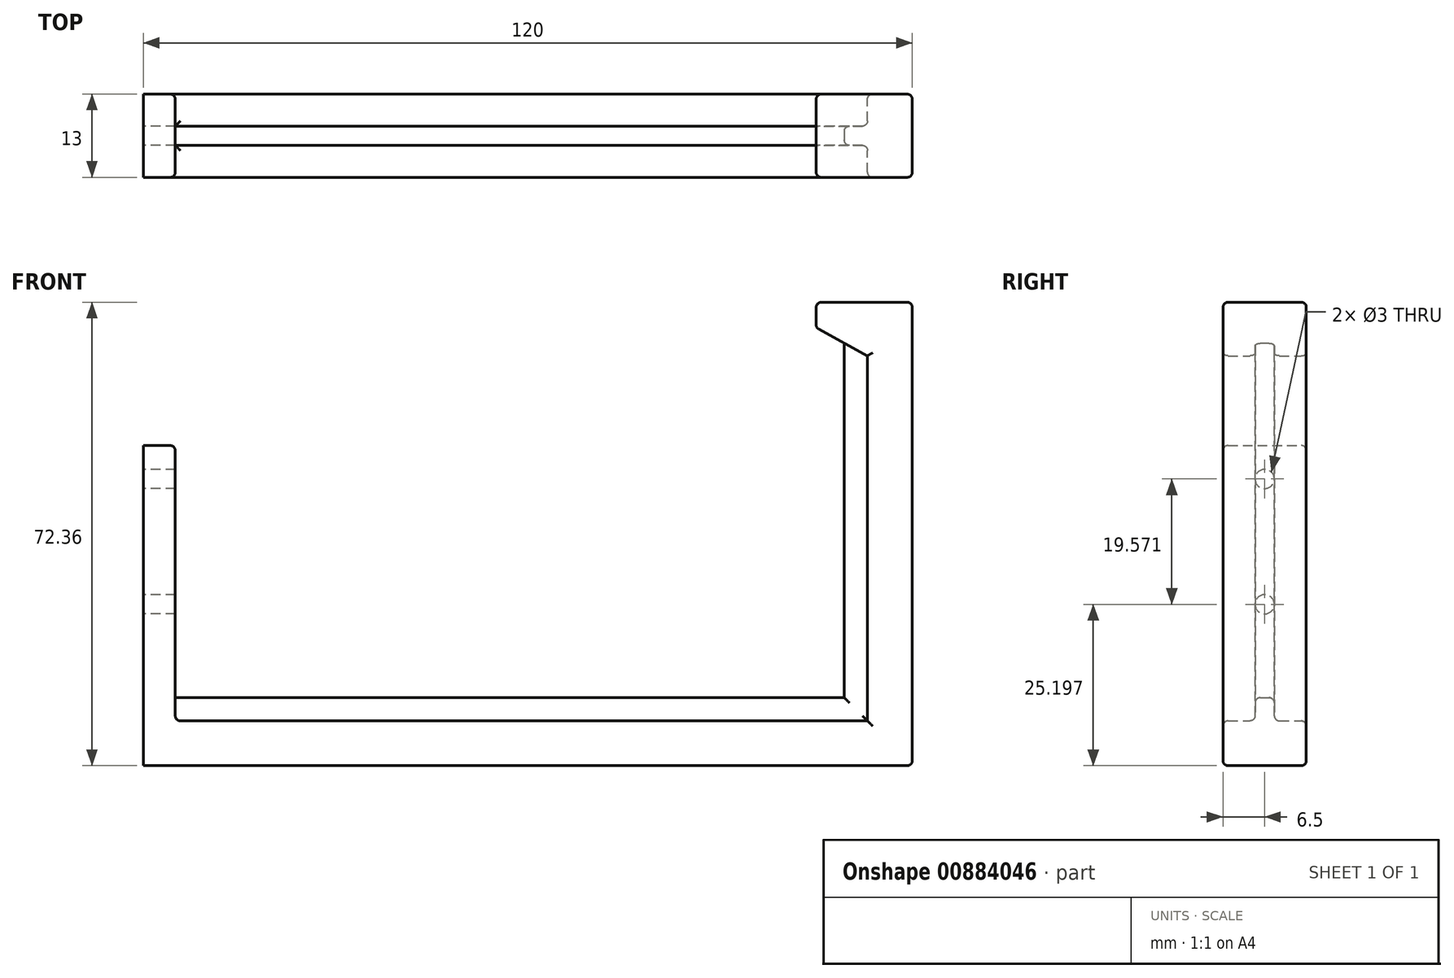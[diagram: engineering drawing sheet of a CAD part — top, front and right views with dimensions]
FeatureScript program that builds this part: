
annotation { "Feature Type Name" : "Feature", "Feature Type Description" : "" }
export const myFeature = defineFeature(function(context is Context, id is Id, definition is map)
    precondition{}
    {
        {
            var Q0;
            Q0=qCreatedBy(makeId("Front.planeOp"),FACE);
            var sketch = newSketch(context, id + "F0", { "sketchPlane" : qUnion([Q0])});
            skLineSegment(sketch, "E0", {"start": v(-72.96, 0) * mm, "end": v(-72.96, 50) * mm});
            skLineSegment(sketch, "E1", {"start": v(-72.96, 50) * mm, "end": v(-67.96, 50) * mm});
            skLineSegment(sketch, "E2", {"start": v(-67.96, 50) * mm, "end": v(-67.96, 7) * mm});
            skLineSegment(sketch, "E3", {"start": v(-67.96, 7) * mm, "end": v(40.04, 7) * mm});
            skLineSegment(sketch, "E4", {"start": v(40.04, 7) * mm, "end": v(40.04, 64) * mm});
            skLineSegment(sketch, "E5", {"start": v(40.04, 64) * mm, "end": v(32.04, 68.36) * mm});
            skLineSegment(sketch, "E6", {"start": v(32.04, 68.36) * mm, "end": v(32.04, 72.36) * mm});
            skLineSegment(sketch, "E7", {"start": v(32.04, 72.36) * mm, "end": v(47.04, 72.36) * mm});
            skLineSegment(sketch, "E8", {"start": v(47.04, 72.36) * mm, "end": v(47.04, 0) * mm});
            skLineSegment(sketch, "E9", {"start": v(47.04, 0) * mm, "end": v(-72.96, 0) * mm});
            skSolve(sketch);
        }
        {
            var Q0;
            Q0=makeQuery(id+"F0.imprint","IMPRINT",FACE,{"disambiguationData":[TD([[makeQuery(id+"F0.imprint","IMPRINT",EDGE,{"derivedFrom":sQuery(id+"F0.wireOp",EDGE,"E0")}),-1.0]])]});
            extrude(context, id + "F1", {"entities" : qUnion([Q0]), "endBound" : BoundingType.SYMMETRIC, "depth" : 13 * mm, "offsetDistance" : 25 * mm});
        }
        {
            var Q0;
            Q0=makeQuery(id+"F1.opExtrude","SWEPT_FACE",FACE,{"disambiguationData":[OSD([sQuery(id+"F0.wireOp",EDGE,"E0")])]});
            var sketch = newSketch(context, id + "F2", { "sketchPlane" : qUnion([Q0])});
            skCircle(sketch, "E10", {"center": v(0, 25.2) * mm, "radius": 1.5 * mm});
            skCircle(sketch, "E11", {"center": v(0, 44.77) * mm, "radius": 1.5 * mm});
            skSolve(sketch);
        }
        {
            var Q0;
            Q0 = qSketchRegion(id + "F2", true);
            extrude(context, id + "F3", {"entities" : qUnion([Q0]), "operationType" : NewBodyOperationType.REMOVE, "oppositeDirection" : true, "depth" : 25 * mm, "offsetDistance" : 25 * mm});
        }
        {
            var Q0;
            Q0=qCreatedBy(makeId("Front.planeOp"),FACE);
            var sketch = newSketch(context, id + "F4", { "sketchPlane" : qUnion([Q0])});
            skLineSegment(sketch, "E12", {"start": v(-71.5, 7.55) * mm, "end": v(-71.5, 5.62) * mm});
            skLineSegment(sketch, "E13", {"start": v(-71.5, 5.62) * mm, "end": v(41.44, 5.62) * mm});
            skLineSegment(sketch, "E14", {"start": v(41.44, 5.62) * mm, "end": v(41.44, 70.86) * mm});
            skLineSegment(sketch, "E15", {"start": v(41.44, 70.86) * mm, "end": v(36.44, 70.86) * mm});
            skLineSegment(sketch, "E16", {"start": v(36.44, 70.86) * mm, "end": v(36.44, 10.62) * mm});
            skLineSegment(sketch, "E17", {"start": v(36.44, 10.62) * mm, "end": v(-71.5, 10.62) * mm});
            skLineSegment(sketch, "E18", {"start": v(-71.5, 7.55) * mm, "end": v(-71.5, 10.62) * mm});
            skSolve(sketch);
        }
        {
            var Q0;
            Q0 = qSketchRegion(id + "F4", true);
            extrude(context, id + "F5", {"entities" : qUnion([Q0]), "operationType" : NewBodyOperationType.ADD, "endBound" : BoundingType.SYMMETRIC, "depth" : 3 * mm, "offsetDistance" : 25 * mm});
        }
        {
            var Q0;
            Q0=makeQuery(id+"F1.opExtrude","CAP_EDGE",EDGE,{"disambiguationData":[OSD([sQuery(id+"F0.wireOp",EDGE,"E2")])],"isStart":false});
            var Q1;
            Q1=makeQuery(id+"F1.opExtrude","SWEPT_EDGE",EDGE,{"disambiguationData":[OSD([sQuery(id+"F0.wireOp",EDGE,"E1"),sQuery(id+"F0.wireOp",EDGE,"E2")])]});
            var Q2;
            Q2=makeQuery(id+"F1.opExtrude","CAP_EDGE",EDGE,{"disambiguationData":[OSD([sQuery(id+"F0.wireOp",EDGE,"E1")])],"isStart":true});
            var Q3;
            Q3=makeQuery(id+"F1.opExtrude","CAP_EDGE",EDGE,{"disambiguationData":[OSD([sQuery(id+"F0.wireOp",EDGE,"E1")])],"isStart":false});
            var Q4;
            Q4=makeQuery(id+"F1.opExtrude","CAP_EDGE",EDGE,{"disambiguationData":[OSD([sQuery(id+"F0.wireOp",EDGE,"E2")])],"isStart":true});
            var Q5;
            Q5=makeQuery(id+"F1.opExtrude","CAP_EDGE",EDGE,{"disambiguationData":[OSD([sQuery(id+"F0.wireOp",EDGE,"E3")])],"isStart":true});
            var Q6;
            Q6=makeQuery(id+"F5.opExtrude","CAP_EDGE",EDGE,{"disambiguationData":[OSD([sQuery(id+"F4.wireOp",EDGE,"E17")])],"isStart":true});
            var Q7;
            Q7=makeQuery(id+"F5.opExtrude","CAP_EDGE",EDGE,{"disambiguationData":[OSD([sQuery(id+"F4.wireOp",EDGE,"E17")])],"isStart":false});
            var Q8;
            Q8=makeQuery(id+"F1.opExtrude","CAP_EDGE",EDGE,{"disambiguationData":[OSD([sQuery(id+"F0.wireOp",EDGE,"E3")])],"isStart":false});
            var Q9;
            Q9=makeQuery(id+"F1.opExtrude","CAP_EDGE",EDGE,{"disambiguationData":[OSD([sQuery(id+"F0.wireOp",EDGE,"E4")])],"isStart":false});
            var Q10;
            Q10=makeQuery(id+"F5.opExtrude","CAP_EDGE",EDGE,{"disambiguationData":[OSD([sQuery(id+"F4.wireOp",EDGE,"E16")])],"isStart":false});
            var Q11;
            Q11=makeQuery(id+"F5.opExtrude","CAP_EDGE",EDGE,{"disambiguationData":[OSD([sQuery(id+"F4.wireOp",EDGE,"E16")])],"isStart":true});
            var Q12;
            Q12=makeQuery(id+"F1.opExtrude","CAP_EDGE",EDGE,{"disambiguationData":[OSD([sQuery(id+"F0.wireOp",EDGE,"E4")])],"isStart":true});
            var Q13;
            Q13=makeQuery(id+"F1.opExtrude","CAP_EDGE",EDGE,{"disambiguationData":[OSD([sQuery(id+"F0.wireOp",EDGE,"E8")])],"isStart":true});
            var Q14;
            Q14=makeQuery(id+"F1.opExtrude","CAP_EDGE",EDGE,{"disambiguationData":[OSD([sQuery(id+"F0.wireOp",EDGE,"E9")])],"isStart":true});
            var Q15;
            Q15=makeQuery(id+"F1.opExtrude","CAP_EDGE",EDGE,{"disambiguationData":[OSD([sQuery(id+"F0.wireOp",EDGE,"E9")])],"isStart":false});
            var Q16;
            Q16=makeQuery(id+"F1.opExtrude","CAP_EDGE",EDGE,{"disambiguationData":[OSD([sQuery(id+"F0.wireOp",EDGE,"E8")])],"isStart":false});
            var Q17;
            Q17=makeQuery(id+"F1.opExtrude","SWEPT_EDGE",EDGE,{"disambiguationData":[OSD([sQuery(id+"F0.wireOp",EDGE,"E7"),sQuery(id+"F0.wireOp",EDGE,"E8")])]});
            var Q18;
            Q18=makeQuery(id+"F1.opExtrude","SWEPT_EDGE",EDGE,{"disambiguationData":[OSD([sQuery(id+"F0.wireOp",EDGE,"E6"),sQuery(id+"F0.wireOp",EDGE,"E7")])]});
            var Q19;
            Q19=makeQuery(id+"F1.opExtrude","CAP_EDGE",EDGE,{"disambiguationData":[OSD([sQuery(id+"F0.wireOp",EDGE,"E7")])],"isStart":true});
            var Q20;
            Q20=makeQuery(id+"F1.opExtrude","CAP_EDGE",EDGE,{"disambiguationData":[OSD([sQuery(id+"F0.wireOp",EDGE,"E7")])],"isStart":false});
            var Q21;
            Q21=makeQuery(id+"F1.opExtrude","SWEPT_EDGE",EDGE,{"disambiguationData":[OSD([sQuery(id+"F0.wireOp",EDGE,"E5"),sQuery(id+"F0.wireOp",EDGE,"E6")])]});
            var Q22;
            Q22=makeQuery(id+"F1.opExtrude","CAP_EDGE",EDGE,{"disambiguationData":[OSD([sQuery(id+"F0.wireOp",EDGE,"E5")])],"isStart":false});
            var Q23;
            Q23=makeQuery(id+"F1.opExtrude","CAP_EDGE",EDGE,{"disambiguationData":[OSD([sQuery(id+"F0.wireOp",EDGE,"E5")])],"isStart":true});
            var Q24;
            Q24=makeQuery(id+"F5.boolean.opBoolean","INTERSECT",EDGE,{"derivedFrom":[makeQuery(id+"F1.opExtrude","SWEPT_FACE",FACE,{"disambiguationData":[OSD([sQuery(id+"F0.wireOp",EDGE,"E4")])]}),makeQuery(id+"F5.opExtrude","CAP_FACE",FACE,{"disambiguationData":[OSD([sQuery(id+"F4.wireOp",EDGE,"E12"),sQuery(id+"F4.wireOp",EDGE,"E13"),sQuery(id+"F4.wireOp",EDGE,"E14"),sQuery(id+"F4.wireOp",EDGE,"E15"),sQuery(id+"F4.wireOp",EDGE,"E16"),sQuery(id+"F4.wireOp",EDGE,"E17"),sQuery(id+"F4.wireOp",EDGE,"E18")])],"isStart":true})]});
            var Q25;
            Q25=makeQuery(id+"F5.boolean.opBoolean","INTERSECT",EDGE,{"derivedFrom":[makeQuery(id+"F1.opExtrude","SWEPT_FACE",FACE,{"disambiguationData":[OSD([sQuery(id+"F0.wireOp",EDGE,"E4")])]}),makeQuery(id+"F5.opExtrude","CAP_FACE",FACE,{"disambiguationData":[OSD([sQuery(id+"F4.wireOp",EDGE,"E12"),sQuery(id+"F4.wireOp",EDGE,"E13"),sQuery(id+"F4.wireOp",EDGE,"E14"),sQuery(id+"F4.wireOp",EDGE,"E15"),sQuery(id+"F4.wireOp",EDGE,"E16"),sQuery(id+"F4.wireOp",EDGE,"E17"),sQuery(id+"F4.wireOp",EDGE,"E18")])],"isStart":false})]});
            var Q26;
            Q26=makeQuery(id+"F1.opExtrude","CAP_EDGE",EDGE,{"disambiguationData":[OSD([sQuery(id+"F0.wireOp",EDGE,"E6")])],"isStart":false});
            var Q27;
            Q27=makeQuery(id+"F1.opExtrude","CAP_EDGE",EDGE,{"disambiguationData":[OSD([sQuery(id+"F0.wireOp",EDGE,"E6")])],"isStart":true});
            var Q28;
            Q28=makeQuery(id+"F5.boolean.opBoolean","INTERSECT",EDGE,{"derivedFrom":[makeQuery(id+"F1.opExtrude","SWEPT_FACE",FACE,{"disambiguationData":[OSD([sQuery(id+"F0.wireOp",EDGE,"E3")])]}),makeQuery(id+"F5.opExtrude","CAP_FACE",FACE,{"disambiguationData":[OSD([sQuery(id+"F4.wireOp",EDGE,"E12"),sQuery(id+"F4.wireOp",EDGE,"E13"),sQuery(id+"F4.wireOp",EDGE,"E14"),sQuery(id+"F4.wireOp",EDGE,"E15"),sQuery(id+"F4.wireOp",EDGE,"E16"),sQuery(id+"F4.wireOp",EDGE,"E17"),sQuery(id+"F4.wireOp",EDGE,"E18")])],"isStart":false})]});
            var Q29;
            Q29=makeQuery(id+"F5.boolean.opBoolean","INTERSECT",EDGE,{"derivedFrom":[makeQuery(id+"F1.opExtrude","SWEPT_FACE",FACE,{"disambiguationData":[OSD([sQuery(id+"F0.wireOp",EDGE,"E3")])]}),makeQuery(id+"F5.opExtrude","CAP_FACE",FACE,{"disambiguationData":[OSD([sQuery(id+"F4.wireOp",EDGE,"E12"),sQuery(id+"F4.wireOp",EDGE,"E13"),sQuery(id+"F4.wireOp",EDGE,"E14"),sQuery(id+"F4.wireOp",EDGE,"E15"),sQuery(id+"F4.wireOp",EDGE,"E16"),sQuery(id+"F4.wireOp",EDGE,"E17"),sQuery(id+"F4.wireOp",EDGE,"E18")])],"isStart":true})]});
            var Q30;
            Q30=makeQuery(id+"F1.opExtrude","SWEPT_EDGE",EDGE,{"disambiguationData":[OSD([sQuery(id+"F0.wireOp",EDGE,"E8"),sQuery(id+"F0.wireOp",EDGE,"E9")])]});
            var Q31;
            {var subQ0=sQuery(id+"F0.wireOp",EDGE,"E3");var subQ1=sQuery(id+"F0.wireOp",EDGE,"E2");Q31=makeQuery(id+"F5.boolean.opBoolean","SPLIT",EDGE,{"disambiguationData":[TD([makeQuery(id+"F5.opExtrude","CAP_FACE",FACE,{"disambiguationData":[OSD([sQuery(id+"F4.wireOp",EDGE,"E12"),sQuery(id+"F4.wireOp",EDGE,"E13"),sQuery(id+"F4.wireOp",EDGE,"E14"),sQuery(id+"F4.wireOp",EDGE,"E15"),sQuery(id+"F4.wireOp",EDGE,"E16"),sQuery(id+"F4.wireOp",EDGE,"E17"),sQuery(id+"F4.wireOp",EDGE,"E18")])],"isStart":false})])],"derivedFrom":makeQuery(id+"F1.opExtrude","SWEPT_EDGE",EDGE,{"disambiguationData":[OSD([subQ1,subQ0])]})});}
            var Q32;
            {var subQ0=sQuery(id+"F0.wireOp",EDGE,"E3");var subQ1=sQuery(id+"F0.wireOp",EDGE,"E2");Q32=makeQuery(id+"F5.boolean.opBoolean","SPLIT",EDGE,{"disambiguationData":[TD([makeQuery(id+"F5.opExtrude","CAP_FACE",FACE,{"disambiguationData":[OSD([sQuery(id+"F4.wireOp",EDGE,"E12"),sQuery(id+"F4.wireOp",EDGE,"E13"),sQuery(id+"F4.wireOp",EDGE,"E14"),sQuery(id+"F4.wireOp",EDGE,"E15"),sQuery(id+"F4.wireOp",EDGE,"E16"),sQuery(id+"F4.wireOp",EDGE,"E17"),sQuery(id+"F4.wireOp",EDGE,"E18")])],"isStart":true})])],"derivedFrom":makeQuery(id+"F1.opExtrude","SWEPT_EDGE",EDGE,{"disambiguationData":[OSD([subQ1,subQ0])]})});}
            fillet(context, id + "F6", {"entities" : qUnion([Q0, Q1, Q2, Q3, Q4, Q5, Q6, Q7, Q8, Q9, Q10, Q11, Q12, Q13, Q14, Q15, Q16, Q17, Q18, Q19, Q20, Q21, Q22, Q23, Q24, Q25, Q26, Q27, Q28, Q29, Q30, Q31, Q32]), "radius" : 0.8 * mm, "tangentPropagation" : true, "allowEdgeOverflow" : false});
        }
    });
